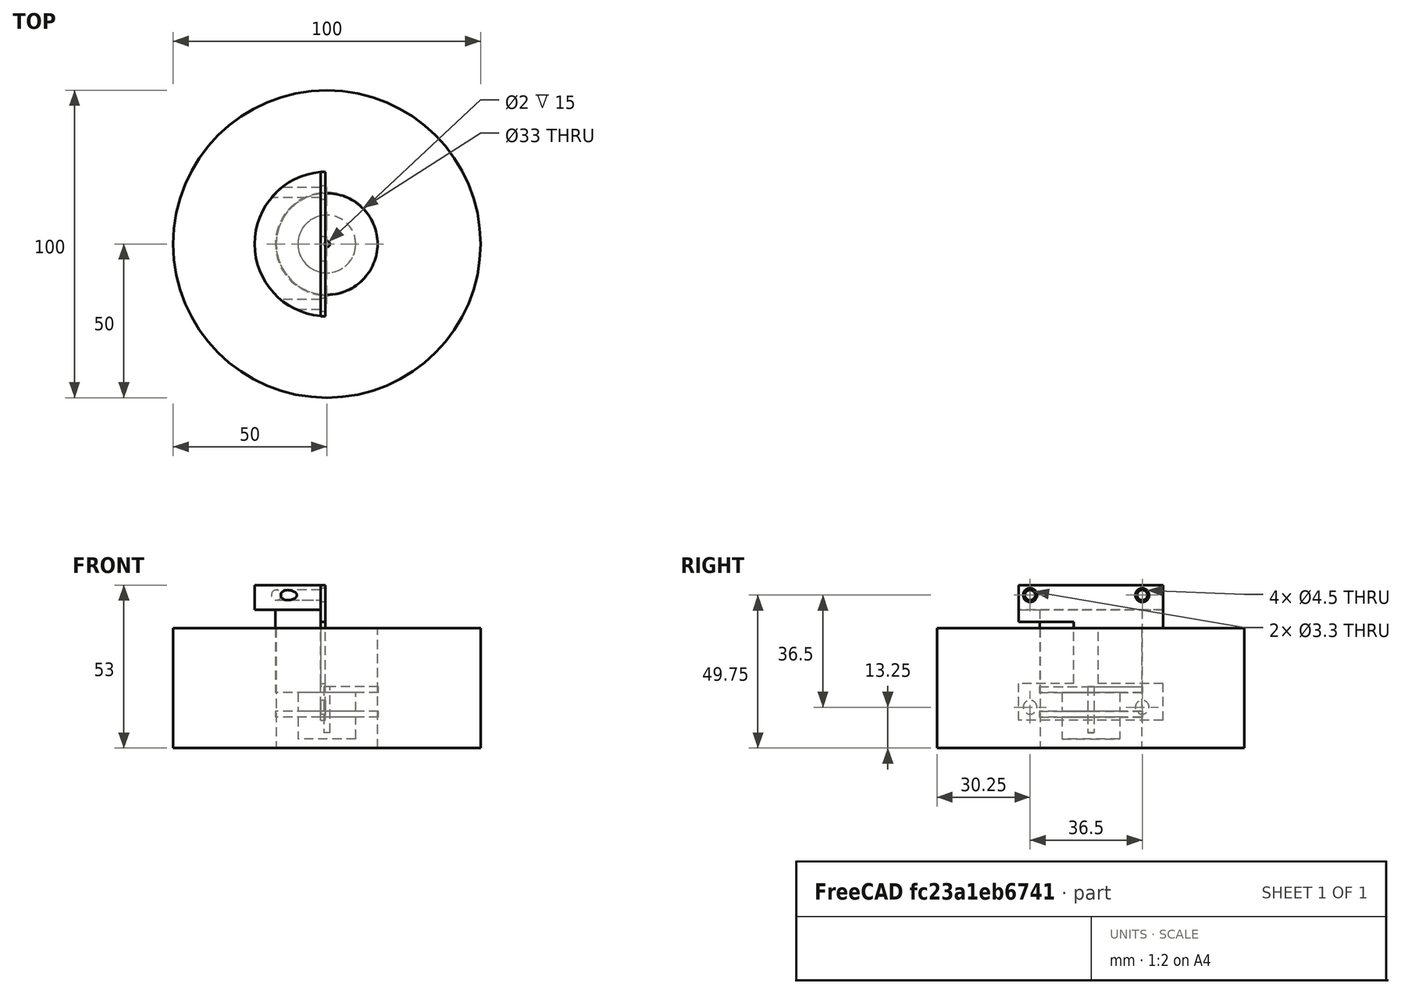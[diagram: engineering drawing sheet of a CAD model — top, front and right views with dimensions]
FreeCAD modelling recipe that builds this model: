
FCSTD DOCUMENT  (FreeCAD 0.20R29603 (Git))
Label: Quak_XL30_PCBHolder02
License: All rights reserved
LicenseURL: http://en.wikipedia.org/wiki/All_rights_reserved
objects: TechDraw::DrawViewDimension×19, Part::Cylinder×15, Part::Cut×8, TechDraw::DrawProjGroupItem×6, Part::Box×4, Part::Compound×4, Part::MultiFuse×2, App::Link×1, TechDraw::DrawSVGTemplate×1, Part::Feature×1, TechDraw::DrawProjGroup×1, TechDraw::DrawPage×1
note: 34 computed .brp shape members not serialized (recipe doc carries the construction recipe); baked Part::Feature solids carry a one-line shape summary decoded from their .brp
EXTERNAL_REF file=PhilippsXL30_SampleMountAdapter_M4to19mm.FCStd obj=Fusion_solid

FEATURE [App::Link] Link  label="PhilippsXL30_SampleMountAdapter_M4to19mm"
  LinkedObject = -> <external PhilippsXL30_SampleMountAdapter_M4to19mm.FCStd>#Fusion_solid
FEATURE [Part::Cylinder] Cylinder  label="Zylinder"
  Angle = 360
  AttacherType = Attacher::AttachEngine3D
  FirstAngle = 0
  Height = 39
  Radius = 50
  SecondAngle = 0
FEATURE [Part::Cylinder] Cylinder001  label="Zylinder001"
  Angle = 360
  AttacherType = Attacher::AttachEngine3D
  FirstAngle = 0
  Height = 39
  Radius = 16.5
  SecondAngle = 0
FEATURE [Part::Cut] Cut  label="LargeCoil"
  Base = -> Cylinder
  Tool = -> Cylinder001
FEATURE [Part::Box] Box  label="Würfel"
  AttacherType = Attacher::AttachEngine3D
  Height = 1.5
  Length = 44
  Placement = pos=(0,0,0) rot=(0,0,1;1.5708rad)
  Width = 47
FEATURE [Part::Box] Box001  label="Würfel001"
  AttacherType = Attacher::AttachEngine3D
  Height = 10
  Length = 18
  Placement = pos=(-47,12,-1) rot=(0,0,1;0rad)
  Width = 20
FEATURE [Part::Box] Box002  label="Würfel002"
  AttacherType = Attacher::AttachEngine3D
  Height = 10
  Length = 21
  Placement = pos=(-21,12,-1) rot=(0,0,1;0rad)
  Width = 18
FEATURE [Part::Compound] Compound001
  Links = -> [Box001,Box002]
FEATURE [Part::Cylinder] Cylinder002  label="Zylinder002"
  Angle = 360
  AttacherType = Attacher::AttachEngine3D
  FirstAngle = 0
  Height = 10
  Placement = pos=(-6.75,4.25,-1) rot=(0,0,1;0rad)
  Radius = 2.25
  SecondAngle = 0
FEATURE [Part::Cylinder] Cylinder003  label="Zylinder003"
  Angle = 360
  AttacherType = Attacher::AttachEngine3D
  FirstAngle = 0
  Height = 10
  Placement = pos=(-43.25,4.25,-1) rot=(0,0,1;0rad)
  Radius = 2.25
  SecondAngle = 0
FEATURE [Part::Cylinder] Cylinder004  label="Zylinder004"
  Angle = 360
  AttacherType = Attacher::AttachEngine3D
  FirstAngle = 0
  Height = 10
  Placement = pos=(-6.75,40.75,-1) rot=(0,0,1;0rad)
  Radius = 2.25
  SecondAngle = 0
FEATURE [Part::Cylinder] Cylinder005  label="Zylinder005"
  Angle = 360
  AttacherType = Attacher::AttachEngine3D
  FirstAngle = 0
  Height = 10
  Placement = pos=(-43.25,40.75,-1) rot=(0,0,1;0rad)
  Radius = 2.25
  SecondAngle = 0
FEATURE [Part::Compound] Compound
  Links = -> [Cylinder005,Cylinder002,Cylinder003,Cylinder004]
FEATURE [Part::Cut] Cut001
  Base = -> Box
  Tool = -> Compound
FEATURE [Part::Cut] Cut002
  Base = -> Cut001
  Placement = pos=(23.5,2,9) rot=(1,0,0;1.5708rad)
  Tool = -> Compound001
FEATURE [Part::Compound] Compound002  label="PCB"
  Links = -> [Cut002]
  Placement = pos=(0,0,0) rot=(0,0,1;1.5708rad)
FEATURE [Part::Cylinder] Cylinder006  label="Zylinder006"
  Angle = 360
  AttacherType = Attacher::AttachEngine3D
  FirstAngle = 0
  Height = 7
  Placement = pos=(0,0,3) rot=(0,0,1;0rad)
  Radius = 9.4
  SecondAngle = 0
FEATURE [Part::Cylinder] Cylinder007  label="Zylinder007"
  Angle = 360
  AttacherType = Attacher::AttachEngine3D
  FirstAngle = 0
  Height = 10
  Placement = pos=(0,0,10) rot=(0,0,1;0rad)
  Radius = 16.75
  SecondAngle = 0
FEATURE [Part::Cylinder] Cylinder008  label="Zylinder008"
  Angle = 360
  AttacherType = Attacher::AttachEngine3D
  FirstAngle = 0
  Height = 43
  Placement = pos=(0,0,10) rot=(0,0,1;0rad)
  Radius = 16.75
  SecondAngle = 0
FEATURE [Part::Box] Box003  label="Würfel003"
  AttacherType = Attacher::AttachEngine3D
  Height = 100
  Length = 50
  Placement = pos=(-2,-25,0) rot=(0,0,1;0rad)
  Width = 100
FEATURE [Part::Cylinder] Cylinder009  label="Zylinder009"
  Angle = 360
  AttacherType = Attacher::AttachEngine3D
  FirstAngle = 0
  Height = 100
  Placement = pos=(-31,-19.75,49.75) rot=(0,1,0;1.5708rad)
  Radius = 1.65
  SecondAngle = 0
FEATURE [Part::Cylinder] Cylinder010  label="Zylinder010"
  Angle = 360
  AttacherType = Attacher::AttachEngine3D
  FirstAngle = 0
  Height = 100
  Placement = pos=(-31,16.75,49.75) rot=(0,1,0;1.5708rad)
  Radius = 1.65
  SecondAngle = 0
FEATURE [Part::Compound] Compound003
  Links = -> [Cylinder009,Cylinder010]
FEATURE [Part::Cylinder] Cylinder011  label="Zylinder011"
  Angle = 360
  AttacherType = Attacher::AttachEngine3D
  FirstAngle = 0
  Height = 100
  Placement = pos=(0,0,5) rot=(0,0,1;0rad)
  Radius = 1
  SecondAngle = 0
FEATURE [Part::Cylinder] Cylinder012  label="Zylinder012"
  Angle = 360
  AttacherType = Attacher::AttachEngine3D
  FirstAngle = 0
  Height = 8
  Placement = pos=(0,0,45) rot=(0,0,1;0rad)
  Radius = 23.5
  SecondAngle = 0
FEATURE [Part::MultiFuse] Fusion
  Shapes = -> [Cylinder008,Cylinder012]
FEATURE [Part::Cut] Cut003
  Base = -> Fusion
  Tool = -> Box003
FEATURE [Part::Cut] Cut004
  Base = -> Cut003
  Tool = -> Compound003
FEATURE [Part::MultiFuse] Fusion001
  Shapes = -> [Cylinder007,Cylinder006,Cut004]
FEATURE [Part::Cut] Cut005
  Base = -> Fusion001
  Tool = -> Cylinder011
FEATURE [Part::Cylinder] Cylinder013  label="Zylinder013"
  Angle = 360
  AttacherType = Attacher::AttachEngine3D
  FirstAngle = 0
  Height = 6
  Placement = pos=(0,0,12) rot=(0,0,1;0rad)
  Radius = 9.4
  SecondAngle = 0
FEATURE [Part::Cylinder] Cylinder014  label="Zylinder014"
  Angle = 360
  AttacherType = Attacher::AttachEngine3D
  FirstAngle = 0
  Height = 6
  Placement = pos=(0,0,12) rot=(0,0,1;0rad)
  Radius = 16.75
  SecondAngle = 0
FEATURE [Part::Cut] Cut006
  Base = -> Cylinder014
  Tool = -> Cylinder013
FEATURE [Part::Cut] Cut007
  Base = -> Cut005
  Tool = -> Cut006
FEATURE [TechDraw::DrawSVGTemplate] Template
  EditableTexts = Designed_by_Name=Thomas Spielauer; FC-Date=2023-08-07; FC-SC=mm; FC-SH=1; FC-Title=QUAK PCB Holder; Subtitle=For XL30 ESEM with large testcoil
  Height = 210
  Orientation = 1
  Width = 297
FEATURE [Part::Feature] Cut007_solid  label="Cut007 (Solid)"
  shape: bbox 40.25 x 46.83 x 50 mm, 24 faces (baked)
FEATURE [TechDraw::DrawProjGroupItem] ProjItem  label="Front"
  CoarseView = false
  Direction = (1,0,0)
  Focus = 100
  HardHidden = false
  IsoCount = 0
  IsoHidden = false
  IsoVisible = false
  LockPosition = true
  Perspective = false
  Rotation = 0
  RotationVector = (0,1,0)
  ScaleType = 2
  SeamHidden = false
  SeamVisible = true
  SmoothHidden = false
  SmoothVisible = true
  Source = -> [Cut007_solid]
  Type = 0
  X = 0
  XDirection = (0,1,0)
  Y = 0
FEATURE [TechDraw::DrawProjGroupItem] ProjItem001  label="Right"
  CoarseView = false
  Direction = (1e-16,1,0)
  Focus = 100
  HardHidden = false
  IsoCount = 0
  IsoHidden = false
  IsoVisible = false
  LockPosition = false
  Perspective = false
  Rotation = 0
  RotationVector = (1,0,0)
  ScaleType = 2
  SeamHidden = false
  SeamVisible = true
  SmoothHidden = false
  SmoothVisible = true
  Source = -> [Cut007_solid]
  Type = 2
  X = -61.8295
  XDirection = (-1,1e-16,0)
  Y = 0
FEATURE [TechDraw::DrawProjGroupItem] ProjItem002  label="Left"
  CoarseView = false
  Direction = (1e-16,-1,0)
  Focus = 100
  HardHidden = false
  IsoCount = 0
  IsoHidden = false
  IsoVisible = false
  LockPosition = false
  Perspective = false
  Rotation = 0
  RotationVector = (1,0,0)
  ScaleType = 2
  SeamHidden = false
  SeamVisible = true
  SmoothHidden = false
  SmoothVisible = true
  Source = -> [Cut007_solid]
  Type = 1
  X = 61.8295
  XDirection = (1,1e-16,0)
  Y = 0
FEATURE [TechDraw::DrawProjGroupItem] ProjItem003  label="Top"
  CoarseView = false
  Direction = (0,0,1)
  Focus = 100
  HardHidden = false
  IsoCount = 0
  IsoHidden = false
  IsoVisible = false
  LockPosition = false
  Perspective = false
  Rotation = 0
  RotationVector = (1,0,0)
  ScaleType = 2
  SeamHidden = false
  SeamVisible = true
  SmoothHidden = false
  SmoothVisible = true
  Source = -> [Cut007_solid]
  Type = 4
  X = 0
  XDirection = (0,1,0)
  Y = -65
FEATURE [TechDraw::DrawProjGroupItem] ProjItem004  label="Bottom"
  CoarseView = false
  Direction = (0,0,-1)
  Focus = 100
  HardHidden = false
  IsoCount = 0
  IsoHidden = false
  IsoVisible = false
  LockPosition = false
  Perspective = false
  Rotation = 0
  RotationVector = (1,0,0)
  ScaleType = 2
  SeamHidden = false
  SeamVisible = true
  SmoothHidden = false
  SmoothVisible = true
  Source = -> [Cut007_solid]
  Type = 5
  X = 0
  XDirection = (0,1,0)
  Y = 65
FEATURE [TechDraw::DrawProjGroupItem] ProjItem005  label="FrontBottomLeft"
  CoarseView = false
  Direction = (0.57735,-0.57735,-0.57735)
  Focus = 100
  HardHidden = false
  IsoCount = 0
  IsoHidden = false
  IsoVisible = false
  LockPosition = false
  Perspective = false
  Rotation = 0
  RotationVector = (1,0,0)
  ScaleType = 2
  SeamHidden = false
  SeamVisible = true
  SmoothHidden = false
  SmoothVisible = true
  Source = -> [Cut007_solid]
  Type = 8
  X = 152.14
  XDirection = (0.707107,0.707107,0)
  Y = 63.8335
FEATURE [TechDraw::DrawProjGroup] ProjGroup
  Anchor = -> ProjItem
  AutoDistribute = false
  LockPosition = false
  ProjectionType = 0
  Rotation = 0
  ScaleType = 0
  Source = -> [Cut007_solid]
  Views = -> [ProjItem,ProjItem001,ProjItem002,ProjItem003,ProjItem004,ProjItem005]
  X = 101.779
  Y = 105.513
  spacingX = 15
  spacingY = 15
FEATURE [TechDraw::DrawViewDimension] Dimension
  AngleOverride = false
  Arbitrary = false
  ArbitraryTolerances = false
  EqualTolerance = true
  ExtensionAngle = 0
  FormatSpec = ⌀%.2w
  FormatSpecOverTolerance = %+.2w
  FormatSpecUnderTolerance = %+.2w
  Inverted = false
  LineAngle = 0
  LockPosition = false
  MeasureType = 1
  OverTolerance = 0
  References2D = -> [ProjItem004]
  Rotation = 0
  ScaleType = 0
  TheoreticalExact = false
  Type = 5
  UnderTolerance = 0
  X = 39.7108
  Y = 14.272
FEATURE [TechDraw::DrawViewDimension] Dimension001
  AngleOverride = false
  Arbitrary = false
  ArbitraryTolerances = false
  EqualTolerance = true
  ExtensionAngle = 0
  FormatSpec = ⌀%.2w
  FormatSpecOverTolerance = %+.2w
  FormatSpecUnderTolerance = %+.2w
  Inverted = false
  LineAngle = 0
  LockPosition = false
  MeasureType = 1
  OverTolerance = 0
  References2D = -> [ProjItem004]
  Rotation = 0
  ScaleType = 0
  TheoreticalExact = false
  Type = 5
  UnderTolerance = 0
  X = 37.1995
  Y = 22.4339
FEATURE [TechDraw::DrawViewDimension] Dimension002
  AngleOverride = false
  Arbitrary = false
  ArbitraryTolerances = false
  EqualTolerance = true
  ExtensionAngle = 0
  FormatSpec = ⌀%.2w
  FormatSpecOverTolerance = %+.2w
  FormatSpecUnderTolerance = %+.2w
  Inverted = false
  LineAngle = 0
  LockPosition = false
  MeasureType = 1
  OverTolerance = 0
  References2D = -> [ProjItem004]
  Rotation = 0
  ScaleType = 0
  TheoreticalExact = false
  Type = 5
  UnderTolerance = 0
  X = 51.0119
  Y = 8.77839
FEATURE [TechDraw::DrawViewDimension] Dimension003
  AngleOverride = false
  Arbitrary = false
  ArbitraryTolerances = false
  EqualTolerance = true
  ExtensionAngle = 0
  FormatSpec = %.2w
  FormatSpecOverTolerance = %+.2w
  FormatSpecUnderTolerance = %+.2w
  Inverted = false
  LineAngle = 0
  LockPosition = false
  MeasureType = 1
  OverTolerance = 0
  References2D = -> [ProjItem001]
  Rotation = 0
  ScaleType = 0
  TheoreticalExact = false
  Type = 0
  UnderTolerance = 0
  X = -11.362
  Y = 37.8196
FEATURE [TechDraw::DrawViewDimension] Dimension004
  AngleOverride = false
  Arbitrary = false
  ArbitraryTolerances = false
  EqualTolerance = true
  ExtensionAngle = 0
  FormatSpec = %.2w
  FormatSpecOverTolerance = %+.2w
  FormatSpecUnderTolerance = %+.2w
  Inverted = false
  LineAngle = 0
  LockPosition = false
  MeasureType = 1
  OverTolerance = 0
  References2D = -> [ProjItem001]
  Rotation = 0
  ScaleType = 0
  TheoreticalExact = false
  Type = 0
  UnderTolerance = 0
  X = 9.17568
  Y = 37.6006
FEATURE [TechDraw::DrawViewDimension] Dimension005
  AngleOverride = false
  Arbitrary = false
  ArbitraryTolerances = false
  EqualTolerance = true
  ExtensionAngle = 0
  FormatSpec = %.2w
  FormatSpecOverTolerance = %+.2w
  FormatSpecUnderTolerance = %+.2w
  Inverted = false
  LineAngle = 0
  LockPosition = false
  MeasureType = 1
  OverTolerance = 0
  References2D = -> [ProjItem001]
  Rotation = 0
  ScaleType = 0
  TheoreticalExact = false
  Type = 0
  UnderTolerance = 0
  X = 5.69309
  Y = -43.4533
FEATURE [TechDraw::DrawViewDimension] Dimension006
  AngleOverride = false
  Arbitrary = false
  ArbitraryTolerances = false
  EqualTolerance = true
  ExtensionAngle = 0
  FormatSpec = %.2w
  FormatSpecOverTolerance = %+.2w
  FormatSpecUnderTolerance = %+.2w
  Inverted = false
  LineAngle = 0
  LockPosition = false
  MeasureType = 1
  OverTolerance = 0
  References2D = -> [ProjItem001]
  Rotation = 0
  ScaleType = 0
  TheoreticalExact = false
  Type = 0
  UnderTolerance = 0
  X = -2.74015
  Y = -35.2232
FEATURE [TechDraw::DrawViewDimension] Dimension007
  AngleOverride = false
  Arbitrary = false
  ArbitraryTolerances = false
  EqualTolerance = true
  ExtensionAngle = 0
  FormatSpec = %.2w
  FormatSpecOverTolerance = %+.2w
  FormatSpecUnderTolerance = %+.2w
  Inverted = false
  LineAngle = 0
  LockPosition = false
  MeasureType = 1
  OverTolerance = 0
  References2D = -> [ProjItem001]
  Rotation = 0
  ScaleType = 0
  TheoreticalExact = false
  Type = 0
  UnderTolerance = 0
  X = 32.8721
  Y = -26.2296
FEATURE [TechDraw::DrawViewDimension] Dimension008
  AngleOverride = false
  Arbitrary = false
  ArbitraryTolerances = false
  EqualTolerance = true
  ExtensionAngle = 0
  FormatSpec = %.2w
  FormatSpecOverTolerance = %+.2w
  FormatSpecUnderTolerance = %+.2w
  Inverted = false
  LineAngle = 0
  LockPosition = false
  MeasureType = 1
  OverTolerance = 0
  References2D = -> [ProjItem001]
  Rotation = 0
  ScaleType = 0
  TheoreticalExact = false
  Type = 0
  UnderTolerance = 0
  X = -28.2799
  Y = -15.1373
FEATURE [TechDraw::DrawViewDimension] Dimension009
  AngleOverride = false
  Arbitrary = false
  ArbitraryTolerances = false
  EqualTolerance = true
  ExtensionAngle = 0
  FormatSpec = %.2w
  FormatSpecOverTolerance = %+.2w
  FormatSpecUnderTolerance = %+.2w
  Inverted = false
  LineAngle = 0
  LockPosition = false
  MeasureType = 1
  OverTolerance = 0
  References2D = -> [ProjItem001]
  Rotation = 0
  ScaleType = 0
  TheoreticalExact = false
  Type = 0
  UnderTolerance = 0
  X = 25.8089
  Y = -0.934947
FEATURE [TechDraw::DrawViewDimension] Dimension010
  AngleOverride = false
  Arbitrary = false
  ArbitraryTolerances = false
  EqualTolerance = true
  ExtensionAngle = 0
  FormatSpec = %.2w
  FormatSpecOverTolerance = %+.2w
  FormatSpecUnderTolerance = %+.2w
  Inverted = false
  LineAngle = 0
  LockPosition = false
  MeasureType = 1
  OverTolerance = 0
  References2D = -> [ProjItem001]
  Rotation = 0
  ScaleType = 0
  TheoreticalExact = false
  Type = 0
  UnderTolerance = 0
  X = 35.7712
  Y = 13.9451
FEATURE [TechDraw::DrawViewDimension] Dimension011
  AngleOverride = false
  Arbitrary = false
  ArbitraryTolerances = false
  EqualTolerance = true
  ExtensionAngle = 0
  FormatSpec = %.2w
  FormatSpecOverTolerance = %+.2w
  FormatSpecUnderTolerance = %+.2w
  Inverted = false
  LineAngle = 0
  LockPosition = false
  MeasureType = 1
  OverTolerance = 0
  References2D = -> [ProjItem001]
  Rotation = 0
  ScaleType = 0
  TheoreticalExact = false
  Type = 0
  UnderTolerance = 0
  X = 30.7923
  Y = 33.2911
FEATURE [TechDraw::DrawViewDimension] Dimension012
  AngleOverride = false
  Arbitrary = false
  ArbitraryTolerances = false
  EqualTolerance = true
  ExtensionAngle = 0
  FormatSpec = %.2w
  FormatSpecOverTolerance = %+.2w
  FormatSpecUnderTolerance = %+.2w
  Inverted = false
  LineAngle = 0
  LockPosition = false
  MeasureType = 1
  OverTolerance = 0
  References2D = -> [ProjItem001]
  Rotation = 0
  ScaleType = 0
  TheoreticalExact = false
  Type = 0
  UnderTolerance = 0
  X = -3.59401
  Y = -60.4879
FEATURE [TechDraw::DrawViewDimension] Dimension013
  AngleOverride = false
  Arbitrary = false
  ArbitraryTolerances = false
  EqualTolerance = true
  ExtensionAngle = 0
  FormatSpec = %.2w
  FormatSpecOverTolerance = %+.2w
  FormatSpecUnderTolerance = %+.2w
  Inverted = false
  LineAngle = 0
  LockPosition = false
  MeasureType = 1
  OverTolerance = 0
  References2D = -> [ProjItem]
  Rotation = 0
  ScaleType = 0
  TheoreticalExact = false
  Type = 0
  UnderTolerance = 0
  X = 29.8167
  Y = 13.4633
FEATURE [TechDraw::DrawViewDimension] Dimension014
  AngleOverride = false
  Arbitrary = false
  ArbitraryTolerances = false
  EqualTolerance = true
  ExtensionAngle = 0
  FormatSpec = %.2w
  FormatSpecOverTolerance = %+.2w
  FormatSpecUnderTolerance = %+.2w
  Inverted = false
  LineAngle = 0
  LockPosition = false
  MeasureType = 1
  OverTolerance = 0
  References2D = -> [ProjItem]
  Rotation = 0
  ScaleType = 0
  TheoreticalExact = false
  Type = 0
  UnderTolerance = 0
  X = -9.68665
  Y = 13.6215
FEATURE [TechDraw::DrawViewDimension] Dimension015
  AngleOverride = false
  Arbitrary = false
  ArbitraryTolerances = false
  EqualTolerance = true
  ExtensionAngle = 0
  FormatSpec = %.2w
  FormatSpecOverTolerance = %+.2w
  FormatSpecUnderTolerance = %+.2w
  Inverted = false
  LineAngle = 0
  LockPosition = false
  MeasureType = 1
  OverTolerance = 0
  References2D = -> [ProjItem]
  Rotation = 0
  ScaleType = 0
  TheoreticalExact = false
  Type = 0
  UnderTolerance = 0
  X = 8.08843
  Y = 16.3293
FEATURE [TechDraw::DrawViewDimension] Dimension016
  AngleOverride = false
  Arbitrary = false
  ArbitraryTolerances = false
  EqualTolerance = true
  ExtensionAngle = 0
  FormatSpec = %.2w
  FormatSpecOverTolerance = %+.2w
  FormatSpecUnderTolerance = %+.2w
  Inverted = false
  LineAngle = 0
  LockPosition = false
  MeasureType = 1
  OverTolerance = 0
  References2D = -> [ProjItem]
  Rotation = 0
  ScaleType = 0
  TheoreticalExact = false
  Type = 0
  UnderTolerance = 0
  X = -1.78657
  Y = 33.7652
FEATURE [TechDraw::DrawViewDimension] Dimension017
  AngleOverride = false
  Arbitrary = false
  ArbitraryTolerances = false
  EqualTolerance = true
  ExtensionAngle = 0
  FormatSpec = %.2w
  FormatSpecOverTolerance = %+.2w
  FormatSpecUnderTolerance = %+.2w
  Inverted = false
  LineAngle = 0
  LockPosition = false
  MeasureType = 1
  OverTolerance = 0
  References2D = -> [ProjItem]
  Rotation = 0
  ScaleType = 0
  TheoreticalExact = false
  Type = 0
  UnderTolerance = 0
  X = 37.5058
  Y = 34.6553
FEATURE [TechDraw::DrawViewDimension] Dimension018
  AngleOverride = false
  Arbitrary = false
  ArbitraryTolerances = false
  EqualTolerance = true
  ExtensionAngle = 0
  FormatSpec = ⌀%.2w (2x M4)
  FormatSpecOverTolerance = %+.2w
  FormatSpecUnderTolerance = %+.2w
  Inverted = false
  LineAngle = 0
  LockPosition = false
  MeasureType = 1
  OverTolerance = 0
  References2D = -> [ProjItem]
  Rotation = 0
  ScaleType = 0
  TheoreticalExact = false
  Type = 5
  UnderTolerance = 0
  X = 33.1185
  Y = 42.0539
FEATURE [TechDraw::DrawPage] Page
  KeepUpdated = true
  NextBalloonIndex = 1
  ProjectionType = 0
  Template = -> Template
  Views = -> [ProjGroup,Dimension,Dimension001,Dimension002,Dimension003,Dimension004,Dimension005,Dimension006,Dimension007,Dimension008,Dimension009,Dimension010,Dimension011,Dimension012,Dimension013,Dimension014,Dimension015,Dimension016,Dimension017,Dimension018]
